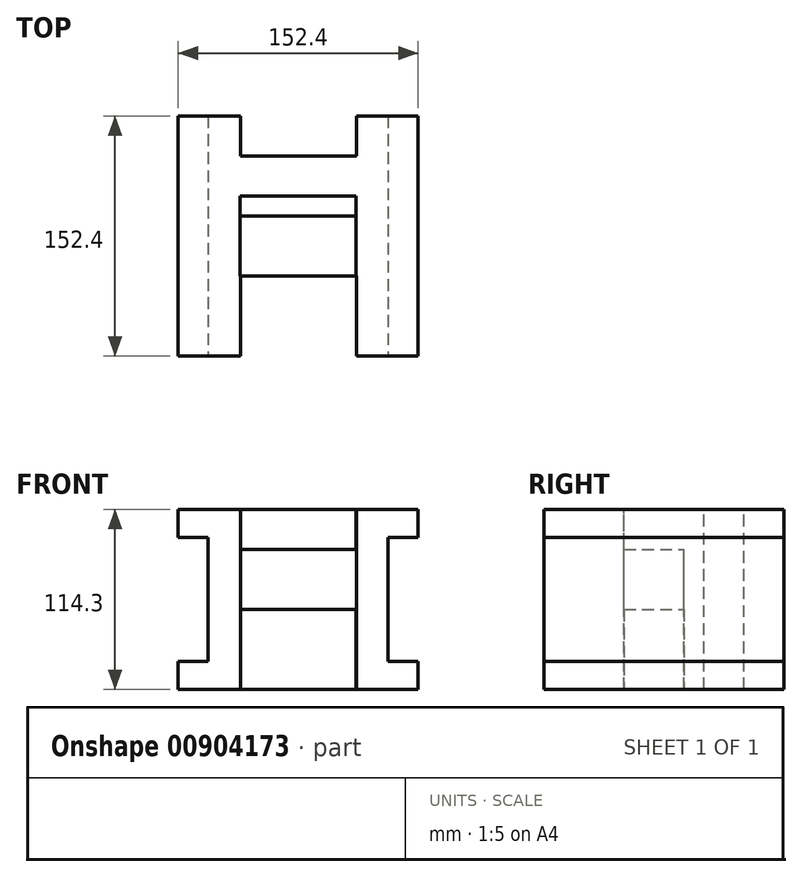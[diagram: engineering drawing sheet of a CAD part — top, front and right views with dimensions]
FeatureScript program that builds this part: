
annotation { "Feature Type Name" : "Feature", "Feature Type Description" : "" }
export const myFeature = defineFeature(function(context is Context, id is Id, definition is map)
    precondition{}
    {
        {
            var Q0;
            Q0=qCreatedBy(makeId("Front.planeOp"),FACE);
            var sketch = newSketch(context, id + "F0", { "sketchPlane" : qUnion([Q0])});
            skLineSegment(sketch, "E0.bottom", {"start": v(-76.2, 57.15) * mm, "end": v(76.2, 57.15) * mm});
            skLineSegment(sketch, "E0.top", {"start": v(-76.2, -57.15) * mm, "end": v(76.2, -57.15) * mm});
            skLineSegment(sketch, "E0.left", {"start": v(-76.2, 57.15) * mm, "end": v(-76.2, -57.15) * mm});
            skLineSegment(sketch, "E0.right", {"start": v(76.2, 57.15) * mm, "end": v(76.2, -57.15) * mm});
            skPoint(sketch, "E0.middle", {"position": v(0, 0) * mm});
            skSolve(sketch);
        }
        {
            var Q0;
            Q0=makeQuery(id+"F0.imprint","IMPRINT",FACE,{"disambiguationData":[TD([[makeQuery(id+"F0.imprint","IMPRINT",EDGE,{"derivedFrom":sQuery(id+"F0.wireOp",EDGE,"E0.bottom")}),-1.0]])]});
            extrude(context, id + "F1", {"entities" : qUnion([Q0]), "depth" : 152.4 * mm, "offsetDistance" : 25.4 * mm});
        }
        {
            var Q0;
            Q0=makeQuery(id+"F1.opExtrude","CAP_FACE",FACE,{"disambiguationData":[OSD([sQuery(id+"F0.wireOp",EDGE,"E0.bottom"),sQuery(id+"F0.wireOp",EDGE,"E0.top"),sQuery(id+"F0.wireOp",EDGE,"E0.left"),sQuery(id+"F0.wireOp",EDGE,"E0.right")])],"isStart":false});
            var sketch = newSketch(context, id + "F2", { "sketchPlane" : qUnion([Q0])});
            skLineSegment(sketch, "E1.bottom", {"start": v(76.2, 39.37) * mm, "end": v(57.15, 39.37) * mm});
            skLineSegment(sketch, "E1.top", {"start": v(76.2, -39.37) * mm, "end": v(57.15, -39.37) * mm});
            skLineSegment(sketch, "E1.left", {"start": v(76.2, 39.37) * mm, "end": v(76.2, -39.37) * mm});
            skLineSegment(sketch, "E1.right", {"start": v(57.15, 39.37) * mm, "end": v(57.15, -39.37) * mm});
            skLineSegment(sketch, "E2.bottom", {"start": v(-76.2, 39.37) * mm, "end": v(-57.15, 39.37) * mm});
            skLineSegment(sketch, "E2.top", {"start": v(-76.2, -39.37) * mm, "end": v(-57.15, -39.37) * mm});
            skLineSegment(sketch, "E2.left", {"start": v(-76.2, 39.37) * mm, "end": v(-76.2, -39.37) * mm});
            skLineSegment(sketch, "E2.right", {"start": v(-57.15, 39.37) * mm, "end": v(-57.15, -39.37) * mm});
            skLineSegment(sketch, "E3", {"start": v(-36.83, 57.15) * mm, "end": v(-36.83, -57.15) * mm});
            skLineSegment(sketch, "E4", {"start": v(36.83, 57.15) * mm, "end": v(36.83, -57.15) * mm});
            skSolve(sketch);
        }
        {
            var Q0;
            Q0=makeQuery(id+"F2.imprint","IMPRINT",FACE,{"disambiguationData":[TD([[makeQuery(id+"F2.imprint","IMPRINT",EDGE,{"derivedFrom":sQuery(id+"F2.wireOp",EDGE,"E2.bottom")}),-1.0]])]});
            extrude(context, id + "F3", {"entities" : qUnion([Q0]), "operationType" : NewBodyOperationType.REMOVE, "endBound" : BoundingType.THROUGH_ALL, "oppositeDirection" : true, "depth" : 25.4 * mm, "offsetDistance" : 25.4 * mm});
        }
        {
            var Q0;
            Q0=makeQuery(id+"F2.imprint","IMPRINT",FACE,{"disambiguationData":[TD([[makeQuery(id+"F2.imprint","IMPRINT",EDGE,{"derivedFrom":sQuery(id+"F2.wireOp",EDGE,"E1.bottom")}),1.0]])]});
            extrude(context, id + "F4", {"entities" : qUnion([Q0]), "operationType" : NewBodyOperationType.REMOVE, "endBound" : BoundingType.THROUGH_ALL, "oppositeDirection" : true, "depth" : 25.4 * mm, "offsetDistance" : 25.4 * mm});
        }
        {
            var Q0;
            Q0=makeQuery(id+"F1.opExtrude","SWEPT_FACE",FACE,{"disambiguationData":[OSD([sQuery(id+"F0.wireOp",EDGE,"E0.bottom")])]});
            var sketch = newSketch(context, id + "F5", { "sketchPlane" : qUnion([Q0])});
            skLineSegment(sketch, "E5.bottom", {"start": v(-36.63, -152.4) * mm, "end": v(37.03, -152.4) * mm});
            skLineSegment(sketch, "E5.top", {"start": v(-36.63, -101.6) * mm, "end": v(37.03, -101.6) * mm});
            skLineSegment(sketch, "E5.left", {"start": v(-36.63, -152.4) * mm, "end": v(-36.63, -101.6) * mm});
            skLineSegment(sketch, "E5.right", {"start": v(37.03, -152.4) * mm, "end": v(37.03, -101.6) * mm});
            skLineSegment(sketch, "E6.bottom", {"start": v(-36.63, 0) * mm, "end": v(37.03, 0) * mm});
            skLineSegment(sketch, "E6.top", {"start": v(-36.63, -25.4) * mm, "end": v(37.03, -25.4) * mm});
            skLineSegment(sketch, "E6.left", {"start": v(-36.63, 0) * mm, "end": v(-36.63, -25.4) * mm});
            skLineSegment(sketch, "E6.right", {"start": v(37.03, 0) * mm, "end": v(37.03, -25.4) * mm});
            skSolve(sketch);
        }
        {
            var Q0;
            Q0 = qSketchRegion(id + "F5", true);
            extrude(context, id + "F6", {"entities" : qUnion([Q0]), "operationType" : NewBodyOperationType.REMOVE, "endBound" : BoundingType.THROUGH_ALL, "oppositeDirection" : true, "depth" : 25.4 * mm, "offsetDistance" : 25.4 * mm});
        }
        {
            var Q0;
            Q0=makeQuery(id+"F5.imprint","IMPRINT",FACE,{"disambiguationData":[TD([[makeQuery(id+"F5.imprint","IMPRINT",EDGE,{"derivedFrom":sQuery(id+"F5.wireOp",EDGE,"E5.top")}),1.0]])]});
            var sketch = newSketch(context, id + "F7", { "sketchPlane" : qUnion([Q0])});
            skLineSegment(sketch, "E7.bottom", {"start": v(-36.83, -101.6) * mm, "end": v(36.83, -101.6) * mm});
            skLineSegment(sketch, "E7.top", {"start": v(-36.83, -50.8) * mm, "end": v(36.83, -50.8) * mm});
            skLineSegment(sketch, "E7.left", {"start": v(-36.83, -101.6) * mm, "end": v(-36.83, -50.8) * mm});
            skLineSegment(sketch, "E7.right", {"start": v(36.83, -101.6) * mm, "end": v(36.83, -50.8) * mm});
            skLineSegment(sketch, "E8", {"start": v(-36.83, -63.5) * mm, "end": v(36.83, -63.5) * mm});
            skSolve(sketch);
        }
        {
            var Q0;
            {var subQ0=sQuery(id+"F7.wireOp",EDGE,"E7.top");Q0=makeQuery(id+"F7.imprint","IMPRINT",FACE,{"disambiguationData":[TD([[makeQuery(id+"F7.imprint","IMPRINT",EDGE,{"derivedFrom":subQ0}),-1.0]])]});}
            extrude(context, id + "F8", {"entities" : qUnion([Q0]), "operationType" : NewBodyOperationType.REMOVE, "endBound" : BoundingType.THROUGH_ALL, "oppositeDirection" : true, "depth" : 25.4 * mm, "offsetDistance" : 25.4 * mm});
        }
        {
            var Q0;
            {var subQ3=sQuery(id+"F7.wireOp",EDGE,"E8");Q0=makeQuery(id+"F7.imprint","IMPRINT",FACE,{"disambiguationData":[TD([[makeQuery(id+"F7.imprint","IMPRINT",EDGE,{"derivedFrom":subQ3}),-1.0]])]});}
            extrude(context, id + "F9", {"entities" : qUnion([Q0]), "operationType" : NewBodyOperationType.REMOVE, "oppositeDirection" : true, "depth" : 25.4 * mm, "offsetDistance" : 25.4 * mm});
        }
        {
            var Q0;
            Q0=makeQuery(id+"F1.opExtrude","SWEPT_FACE",FACE,{"disambiguationData":[OSD([sQuery(id+"F0.wireOp",EDGE,"E0.top")])]});
            var sketch = newSketch(context, id + "F10", { "sketchPlane" : qUnion([Q0])});
            skLineSegment(sketch, "E9.bottom", {"start": v(-36.63, 101.6) * mm, "end": v(36.83, 101.6) * mm});
            skLineSegment(sketch, "E9.top", {"start": v(-36.63, 63.5) * mm, "end": v(36.83, 63.5) * mm});
            skLineSegment(sketch, "E9.left", {"start": v(-36.63, 101.6) * mm, "end": v(-36.63, 63.5) * mm});
            skLineSegment(sketch, "E9.right", {"start": v(36.83, 101.6) * mm, "end": v(36.83, 63.5) * mm});
            skSolve(sketch);
        }
        {
            var Q0;
            Q0=makeQuery(id+"F10.imprint","IMPRINT",FACE,{"disambiguationData":[TD([[makeQuery(id+"F10.imprint","IMPRINT",EDGE,{"derivedFrom":sQuery(id+"F10.wireOp",EDGE,"E9.bottom")}),-1.0]])]});
            extrude(context, id + "F11", {"entities" : qUnion([Q0]), "operationType" : NewBodyOperationType.REMOVE, "oppositeDirection" : true, "depth" : 50.8 * mm, "offsetDistance" : 25.4 * mm});
        }
    });
